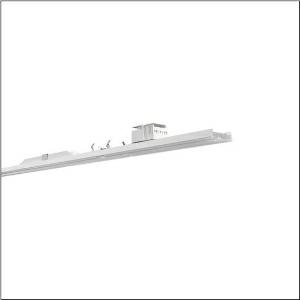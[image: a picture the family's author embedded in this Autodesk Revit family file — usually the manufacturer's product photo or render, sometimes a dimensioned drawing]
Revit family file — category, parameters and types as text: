
# Revit family: licross_r__11_recessed_mo_51tl11cn48xf_63ce
name_source: partatom
category: Lighting Fixtures
units: mm (PartAtom-declared; Revit-internal decimal feet)

## family parameters
Cut with Voids When Loaded = No
Host = Face
Light Source = No
Part Type = Normal
Room Calculation Point = No
Round Connector Dimension = Use Diameter
Shared = No

## types (1)
- --- (1 x LED, 8170 lm, 48 W, 4000K)
    Apparent Load = 48 VA
    CIE Flux Codes = 89 96 99 100 100
    Color Rendering = 80
    Color Temperature = 4000K
    Default Elevation = 1800 mm
    Description = Licross® 11 Recessed MOluminaire insert, length: 1.500mm, width: 66mm, height: 67mm, LED rated luminous flux: 8.170lm, light colour: 840, control gear: ON/OFF Multilumen, CLOi, control gear: ECG Multilumen, with plug, 3-pole, with phase selection, mains connection: 220..240V, AC, 50/60Hz, halogen-free wiring, primary optical cover: cover, of PMMA, light emission: direct distribution, protection rating (complete): IP40, insulation class (complete): insulation class I (protective earthing), certification: CE, ENEC, VDE, protection symbol: D if used in an environment without relevant dust loads with corresponding accessories, permissible ambient temperature for indoor applications: -35..+40°C, reducing of maximum allowable ambient temperature of 5°C with ceiling mounting, corresponds to IFS (International Featured Standards) requirements for safety and quality in the food industry, packaging unit: 1 piece
    Height = 58 mm
    Lamp = 1 x LED
    Lamp Light Flux = 8170 lm
    Lamp Power = 48 W
    Lamp count = 1
    Length = 1500 mm
    Luminous efficacy = 170 lm/W
    Manufacturer = Siteco
    ModVariant = No
    Model = 51TL11CN48XF
    Mounting Place = Ceiling
    Mounting Type = Pendant
    Number of Poles = 1
    OnlyDefault = Yes
    Power Factor = 1
    Product Name = Licross® 11 Recessed MO
    Product group = luminaire insert
    ProductGroupID = 902
    Protection Class = Protection class I
    Protection Degree = IP 40
    RLX_Detail_Level = 1
    RlxData = <blob elided: 19997 chars, md5=56465e13>
    Socket = socket
    Standby Power = 0 W
    System Light Flux = 8170 lm
    System Power = 48 W
    Type Comments = factory setting: luminous flux: 100 % | (A | C | E) | 109 mA
    Type Image = l_1266722.jpg
    URL = http://relux.com
    VarID = @adj_138771
    Voltage = 0 V
    Weight = 0.00 kg
    Width = 66 mm

## geometry (parser evidence)
native form markers: Blend x4, Sweep x9
no freeform markers — native parametric forms only
